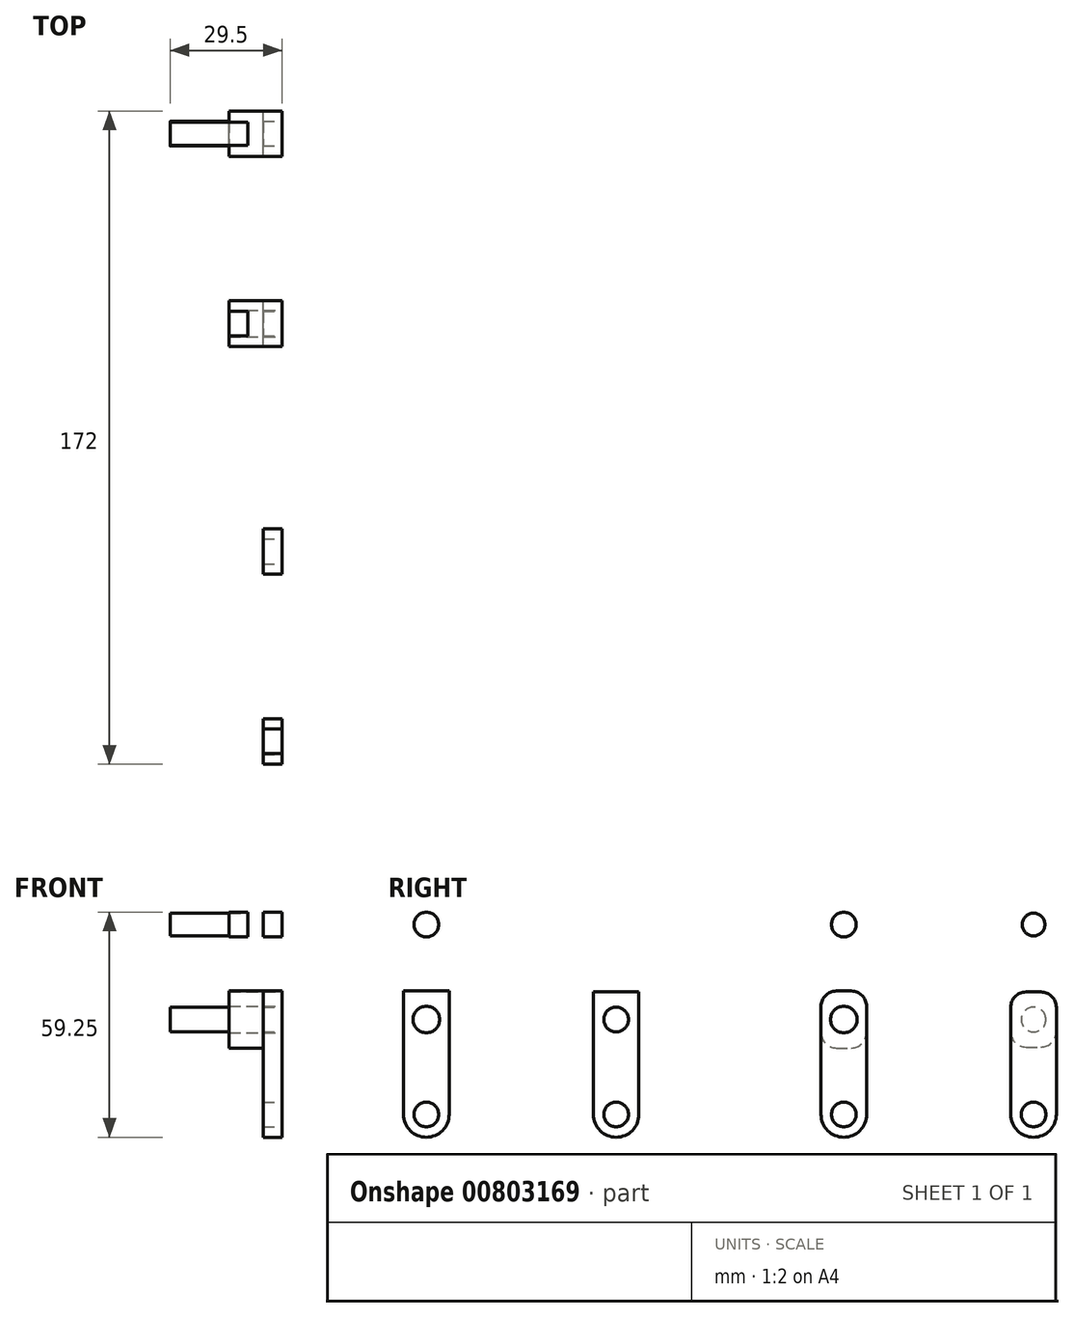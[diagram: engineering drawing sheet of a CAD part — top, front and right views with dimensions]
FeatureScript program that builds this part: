
annotation { "Feature Type Name" : "Feature", "Feature Type Description" : "" }
export const myFeature = defineFeature(function(context is Context, id is Id, definition is map)
    precondition{}
    {
        {
            var Q0;
            Q0=qCreatedBy(makeId("Right.planeOp"),FACE);
            var sketch = newSketch(context, id + "F0", { "sketchPlane" : qUnion([Q0])});
            skCircle(sketch, "E0", {"center": v(0, 0) * mm, "radius": 3.25 * mm});
            skArc(sketch, "E1", {"start": v(-6, 0) * mm, "mid": v(0, -6) * mm, "end": v(6, 0) * mm});
            skLineSegment(sketch, "E2", {"start": v(-6, 0) * mm, "end": v(-6, 25) * mm});
            skLineSegment(sketch, "E3", {"start": v(6, 0) * mm, "end": v(6, 25) * mm});
            skLineSegment(sketch, "E4", {"start": v(-6, 25) * mm, "end": v(6, 25) * mm, "construction": true});
            skLineSegment(sketch, "E5.MirrorCS", {"start": v(6, 50) * mm, "end": v(6, 25) * mm});
            skLineSegment(sketch, "E6.MirrorCS", {"start": v(-6, 50) * mm, "end": v(-6, 25) * mm});
            skArc(sketch, "E7.MirrorCS", {"start": v(-6, 50) * mm, "mid": v(0, 56) * mm, "end": v(6, 50) * mm});
            skCircle(sketch, "E8", {"center": v(0, 25) * mm, "radius": 3.25 * mm});
            skLineSegment(sketch, "E9", {"start": v(-6, 32.25) * mm, "end": v(6, 32.25) * mm});
            skLineSegment(sketch, "E10.MirrorCS", {"start": v(-6, 17.75) * mm, "end": v(6, 17.75) * mm});
            skCircle(sketch, "E11", {"center": v(-50, 0) * mm, "radius": 3.25 * mm});
            skArc(sketch, "E12", {"start": v(-56, 0) * mm, "mid": v(-50, -6) * mm, "end": v(-44, 0) * mm});
            skLineSegment(sketch, "E13", {"start": v(-56, 0) * mm, "end": v(-56, 25) * mm});
            skLineSegment(sketch, "E14", {"start": v(-44, 0) * mm, "end": v(-44, 25) * mm});
            skLineSegment(sketch, "E15", {"start": v(-56, 25) * mm, "end": v(-44, 25) * mm, "construction": true});
            skLineSegment(sketch, "E16.MirrorCS", {"start": v(-44, 50) * mm, "end": v(-44, 25) * mm});
            skLineSegment(sketch, "E17.MirrorCS", {"start": v(-56, 50) * mm, "end": v(-56, 25) * mm});
            skCircle(sketch, "E18.MirrorC", {"center": v(-50, 50) * mm, "radius": 3.25 * mm});
            skArc(sketch, "E19.MirrorCS", {"start": v(-56, 50) * mm, "mid": v(-50, 56) * mm, "end": v(-44, 50) * mm});
            skCircle(sketch, "E20", {"center": v(-50, 25) * mm, "radius": 3.5 * mm});
            skLineSegment(sketch, "E21", {"start": v(-56, 32.5) * mm, "end": v(-44, 32.5) * mm});
            skLineSegment(sketch, "E22.MirrorCS", {"start": v(-56, 17.5) * mm, "end": v(-44, 17.5) * mm});
            skCircle(sketch, "E23", {"center": v(0, 50) * mm, "radius": 3 * mm});
            skCircle(sketch, "E24", {"center": v(-110, 0) * mm, "radius": 3.25 * mm});
            skArc(sketch, "E25", {"start": v(-116, 0) * mm, "mid": v(-110, -6) * mm, "end": v(-104, 0) * mm});
            skLineSegment(sketch, "E26", {"start": v(-116, 0) * mm, "end": v(-116, 25) * mm});
            skLineSegment(sketch, "E27", {"start": v(-104, 0) * mm, "end": v(-104, 25) * mm});
            skLineSegment(sketch, "E28", {"start": v(-116, 25) * mm, "end": v(-104, 25) * mm, "construction": true});
            skLineSegment(sketch, "E29.MirrorCS", {"start": v(-104, 50) * mm, "end": v(-104, 25) * mm});
            skLineSegment(sketch, "E30.MirrorCS", {"start": v(-116, 50) * mm, "end": v(-116, 25) * mm});
            skArc(sketch, "E31.MirrorCS", {"start": v(-116, 50) * mm, "mid": v(-110, 56) * mm, "end": v(-104, 50) * mm});
            skCircle(sketch, "E32", {"center": v(-110, 25) * mm, "radius": 3.25 * mm});
            skLineSegment(sketch, "E33", {"start": v(-116, 32.25) * mm, "end": v(-104, 32.25) * mm});
            skLineSegment(sketch, "E34.MirrorCS", {"start": v(-116, 17.75) * mm, "end": v(-104, 17.75) * mm});
            skCircle(sketch, "E35", {"center": v(-160, 0) * mm, "radius": 3.25 * mm});
            skArc(sketch, "E36", {"start": v(-166, 0) * mm, "mid": v(-160, -6) * mm, "end": v(-154, 0) * mm});
            skLineSegment(sketch, "E37", {"start": v(-166, 0) * mm, "end": v(-166, 25) * mm});
            skLineSegment(sketch, "E38", {"start": v(-154, 0) * mm, "end": v(-154, 25) * mm});
            skLineSegment(sketch, "E39", {"start": v(-166, 25) * mm, "end": v(-154, 25) * mm, "construction": true});
            skLineSegment(sketch, "E40.MirrorCS", {"start": v(-154, 50) * mm, "end": v(-154, 25) * mm});
            skLineSegment(sketch, "E41.MirrorCS", {"start": v(-166, 50) * mm, "end": v(-166, 25) * mm});
            skCircle(sketch, "E42.MirrorC", {"center": v(-160, 50) * mm, "radius": 3.25 * mm});
            skArc(sketch, "E43.MirrorCS", {"start": v(-166, 50) * mm, "mid": v(-160, 56) * mm, "end": v(-154, 50) * mm});
            skCircle(sketch, "E44", {"center": v(-160, 25) * mm, "radius": 3.5 * mm});
            skLineSegment(sketch, "E45", {"start": v(-166, 32.5) * mm, "end": v(-154, 32.5) * mm});
            skLineSegment(sketch, "E46.MirrorCS", {"start": v(-166, 17.5) * mm, "end": v(-154, 17.5) * mm});
            skCircle(sketch, "E47", {"center": v(-110, 50) * mm, "radius": 3 * mm});
            skCircle(sketch, "E48", {"center": v(-220, 0) * mm, "radius": 3.25 * mm});
            skArc(sketch, "E49", {"start": v(-226, 0) * mm, "mid": v(-220, -6) * mm, "end": v(-214, 0) * mm});
            skLineSegment(sketch, "E50", {"start": v(-226, 0) * mm, "end": v(-226, 25) * mm});
            skLineSegment(sketch, "E51", {"start": v(-214, 0) * mm, "end": v(-214, 25) * mm});
            skLineSegment(sketch, "E52", {"start": v(-226, 25) * mm, "end": v(-214, 25) * mm, "construction": true});
            skLineSegment(sketch, "E53.MirrorCS", {"start": v(-214, 50) * mm, "end": v(-214, 25) * mm});
            skLineSegment(sketch, "E54.MirrorCS", {"start": v(-226, 50) * mm, "end": v(-226, 25) * mm});
            skCircle(sketch, "E55.MirrorC", {"center": v(-220, 50) * mm, "radius": 3.25 * mm});
            skArc(sketch, "E56.MirrorCS", {"start": v(-226, 50) * mm, "mid": v(-220, 56) * mm, "end": v(-214, 50) * mm});
            skCircle(sketch, "E57", {"center": v(-220, 25) * mm, "radius": 3.5 * mm});
            skLineSegment(sketch, "E58", {"start": v(-226, 32.5) * mm, "end": v(-214, 32.5) * mm});
            skLineSegment(sketch, "E59.MirrorCS", {"start": v(-226, 17.5) * mm, "end": v(-214, 17.5) * mm});
            skSolve(sketch);
        }
        {
            var Q0;
            Q0=makeQuery(id+"F0.imprint","IMPRINT",FACE,{"disambiguationData":[TD([[makeQuery(id+"F0.imprint","IMPRINT",EDGE,{"derivedFrom":sQuery(id+"F0.wireOp",EDGE,"E0")}),-1.0]])]});
            var Q1;
            Q1=makeQuery(id+"F0.imprint","IMPRINT",FACE,{"disambiguationData":[TD([[makeQuery(id+"F0.imprint","IMPRINT",EDGE,{"derivedFrom":sQuery(id+"F0.wireOp",EDGE,"E8")}),-1.0]])]});
            var Q2;
            Q2=makeQuery(id+"F0.imprint","IMPRINT",FACE,{"disambiguationData":[TD([[makeQuery(id+"F0.imprint","IMPRINT",EDGE,{"derivedFrom":sQuery(id+"F0.wireOp",EDGE,"E11")}),-1.0]])]});
            var Q3;
            Q3=makeQuery(id+"F0.imprint","IMPRINT",FACE,{"disambiguationData":[TD([[makeQuery(id+"F0.imprint","IMPRINT",EDGE,{"derivedFrom":sQuery(id+"F0.wireOp",EDGE,"E20")}),-1.0]])]});
            var Q4;
            Q4=makeQuery(id+"F0.imprint","IMPRINT",FACE,{"disambiguationData":[TD([[makeQuery(id+"F0.imprint","IMPRINT",EDGE,{"derivedFrom":sQuery(id+"F0.wireOp",EDGE,"E24")}),-1.0]])]});
            var Q5;
            Q5=makeQuery(id+"F0.imprint","IMPRINT",FACE,{"disambiguationData":[TD([[makeQuery(id+"F0.imprint","IMPRINT",EDGE,{"derivedFrom":sQuery(id+"F0.wireOp",EDGE,"E32")}),-1.0]])]});
            var Q6;
            {var subQ1=sQuery(id+"F0.wireOp",EDGE,"E31.MirrorCS");Q6=makeQuery(id+"F0.imprint","IMPRINT",FACE,{"disambiguationData":[TD([[makeQuery(id+"F0.imprint","IMPRINT",EDGE,{"derivedFrom":subQ1}),-1.0]])]});}
            var Q7;
            Q7=makeQuery(id+"F0.imprint","IMPRINT",FACE,{"disambiguationData":[TD([[makeQuery(id+"F0.imprint","IMPRINT",EDGE,{"derivedFrom":sQuery(id+"F0.wireOp",EDGE,"E35")}),-1.0]])]});
            var Q8;
            Q8=makeQuery(id+"F0.imprint","IMPRINT",FACE,{"disambiguationData":[TD([[makeQuery(id+"F0.imprint","IMPRINT",EDGE,{"derivedFrom":sQuery(id+"F0.wireOp",EDGE,"E44")}),-1.0]])]});
            var Q9;
            Q9=makeQuery(id+"F0.imprint","IMPRINT",FACE,{"disambiguationData":[TD([[makeQuery(id+"F0.imprint","IMPRINT",EDGE,{"derivedFrom":sQuery(id+"F0.wireOp",EDGE,"E42.MirrorC")}),1.0]])]});
            extrude(context, id + "F1", {"entities" : qUnion([Q0, Q1, Q2, Q3, Q4, Q5, Q6, Q7, Q8, Q9]), "oppositeDirection" : true, "depth" : 5 * mm, "offsetDistance" : 25 * mm});
        }
        {
            var Q0;
            Q0=makeQuery(id+"F0.imprint","IMPRINT",FACE,{"disambiguationData":[TD([[makeQuery(id+"F0.imprint","IMPRINT",EDGE,{"derivedFrom":sQuery(id+"F0.wireOp",EDGE,"E8")}),-1.0]])]});
            var Q1;
            Q1=makeQuery(id+"F0.imprint","IMPRINT",FACE,{"disambiguationData":[TD([[makeQuery(id+"F0.imprint","IMPRINT",EDGE,{"derivedFrom":sQuery(id+"F0.wireOp",EDGE,"E20")}),-1.0]])]});
            extrude(context, id + "F2", {"entities" : qUnion([Q0, Q1]), "operationType" : NewBodyOperationType.ADD, "oppositeDirection" : true, "depth" : (28 / 2) * mm, "offsetDistance" : 25 * mm});
        }
        {
            var Q0;
            Q0=makeQuery(id+"F0.imprint","IMPRINT",FACE,{"disambiguationData":[TD([[makeQuery(id+"F0.imprint","IMPRINT",EDGE,{"derivedFrom":sQuery(id+"F0.wireOp",EDGE,"E8")}),-1.0]])]});
            var Q1;
            {var subQ1=sQuery(id+"F0.wireOp",EDGE,"E7.MirrorCS");Q1=makeQuery(id+"F0.imprint","IMPRINT",FACE,{"disambiguationData":[TD([[makeQuery(id+"F0.imprint","IMPRINT",EDGE,{"derivedFrom":subQ1}),-1.0]])]});}
            var Q2;
            Q2=makeQuery(id+"F0.imprint","IMPRINT",FACE,{"disambiguationData":[TD([[makeQuery(id+"F0.imprint","IMPRINT",EDGE,{"derivedFrom":sQuery(id+"F0.wireOp",EDGE,"E18.MirrorC")}),1.0]])]});
            extrude(context, id + "F3", {"entities" : qUnion([Q0, Q1, Q2]), "operationType" : NewBodyOperationType.ADD, "oppositeDirection" : true, "depth" : (28 / 2) * mm, "offsetDistance" : 25 * mm, "hasSecondDirection" : true, "secondDirectionOppositeDirection" : true, "secondDirectionDepth" : (14 - 5) * mm});
        }
        {
            var Q0;
            Q0=makeQuery(id+"F0.imprint","IMPRINT",FACE,{"disambiguationData":[TD([[makeQuery(id+"F0.imprint","IMPRINT",EDGE,{"derivedFrom":sQuery(id+"F0.wireOp",EDGE,"E8")}),1.0]])]});
            extrude(context, id + "F4", {"entities" : qUnion([Q0]), "operationType" : NewBodyOperationType.ADD, "oppositeDirection" : true, "depth" : (28 + 1.5) * mm, "offsetDistance" : 25 * mm});
        }
        {
            var Q0;
            Q0=makeQuery(id+"F0.imprint","IMPRINT",FACE,{"disambiguationData":[TD([[makeQuery(id+"F0.imprint","IMPRINT",EDGE,{"derivedFrom":sQuery(id+"F0.wireOp",EDGE,"E23")}),1.0]])]});
            extrude(context, id + "F5", {"entities" : qUnion([Q0]), "operationType" : NewBodyOperationType.ADD, "oppositeDirection" : true, "depth" : (28 + 1.5) * mm, "offsetDistance" : 25 * mm, "hasSecondDirection" : true, "secondDirectionOppositeDirection" : true, "secondDirectionDepth" : 9 * mm});
        }
        {
            var Q0;
            {var subQ0=sQuery(id+"F0.wireOp",EDGE,"E9");var subQ1=sQuery(id+"F0.wireOp",EDGE,"E5.MirrorCS");Q0=makeQuery(id+"F2.boolean.opBoolean","MERGE",EDGE,{"derivedFrom":[makeQuery(id+"F1.opExtrude","SWEPT_EDGE",EDGE,{"disambiguationData":[OSD([subQ1,subQ0])]}),makeQuery(id+"F2.opExtrude","SWEPT_EDGE",EDGE,{"disambiguationData":[OSD([subQ1,subQ0])]})]});}
            var Q1;
            {var subQ0=sQuery(id+"F0.wireOp",EDGE,"E9");var subQ1=sQuery(id+"F0.wireOp",EDGE,"E6.MirrorCS");Q1=makeQuery(id+"F2.boolean.opBoolean","MERGE",EDGE,{"derivedFrom":[makeQuery(id+"F1.opExtrude","SWEPT_EDGE",EDGE,{"disambiguationData":[OSD([subQ1,subQ0])]}),makeQuery(id+"F2.opExtrude","SWEPT_EDGE",EDGE,{"disambiguationData":[OSD([subQ1,subQ0])]})]});}
            var Q2;
            Q2=makeQuery(id+"F2.opExtrude","SWEPT_EDGE",EDGE,{"disambiguationData":[OSD([sQuery(id+"F0.wireOp",EDGE,"E2"),sQuery(id+"F0.wireOp",EDGE,"E10.MirrorCS")])]});
            var Q3;
            Q3=makeQuery(id+"F2.opExtrude","SWEPT_EDGE",EDGE,{"disambiguationData":[OSD([sQuery(id+"F0.wireOp",EDGE,"E3"),sQuery(id+"F0.wireOp",EDGE,"E10.MirrorCS")])]});
            var Q4;
            {var subQ0=sQuery(id+"F0.wireOp",EDGE,"E21");var subQ1=sQuery(id+"F0.wireOp",EDGE,"E17.MirrorCS");Q4=makeQuery(id+"F2.boolean.opBoolean","MERGE",EDGE,{"derivedFrom":[makeQuery(id+"F1.opExtrude","SWEPT_EDGE",EDGE,{"disambiguationData":[OSD([subQ1,subQ0])]}),makeQuery(id+"F2.opExtrude","SWEPT_EDGE",EDGE,{"disambiguationData":[OSD([subQ1,subQ0])]})]});}
            var Q5;
            {var subQ0=sQuery(id+"F0.wireOp",EDGE,"E21");var subQ1=sQuery(id+"F0.wireOp",EDGE,"E16.MirrorCS");Q5=makeQuery(id+"F2.boolean.opBoolean","MERGE",EDGE,{"derivedFrom":[makeQuery(id+"F1.opExtrude","SWEPT_EDGE",EDGE,{"disambiguationData":[OSD([subQ1,subQ0])]}),makeQuery(id+"F2.opExtrude","SWEPT_EDGE",EDGE,{"disambiguationData":[OSD([subQ1,subQ0])]})]});}
            var Q6;
            Q6=makeQuery(id+"F2.opExtrude","SWEPT_EDGE",EDGE,{"disambiguationData":[OSD([sQuery(id+"F0.wireOp",EDGE,"E13"),sQuery(id+"F0.wireOp",EDGE,"E22.MirrorCS")])]});
            var Q7;
            Q7=makeQuery(id+"F2.opExtrude","SWEPT_EDGE",EDGE,{"disambiguationData":[OSD([sQuery(id+"F0.wireOp",EDGE,"E14"),sQuery(id+"F0.wireOp",EDGE,"E22.MirrorCS")])]});
            fillet(context, id + "F6", {"entities" : qUnion([Q0, Q1, Q2, Q3, Q4, Q5, Q6, Q7]), "tangentPropagation" : true, "radius" : 4 * mm, "defaultsChanged" : false, "vertexSettings" : [], "allowEdgeOverflow" : false});
        }
    });
